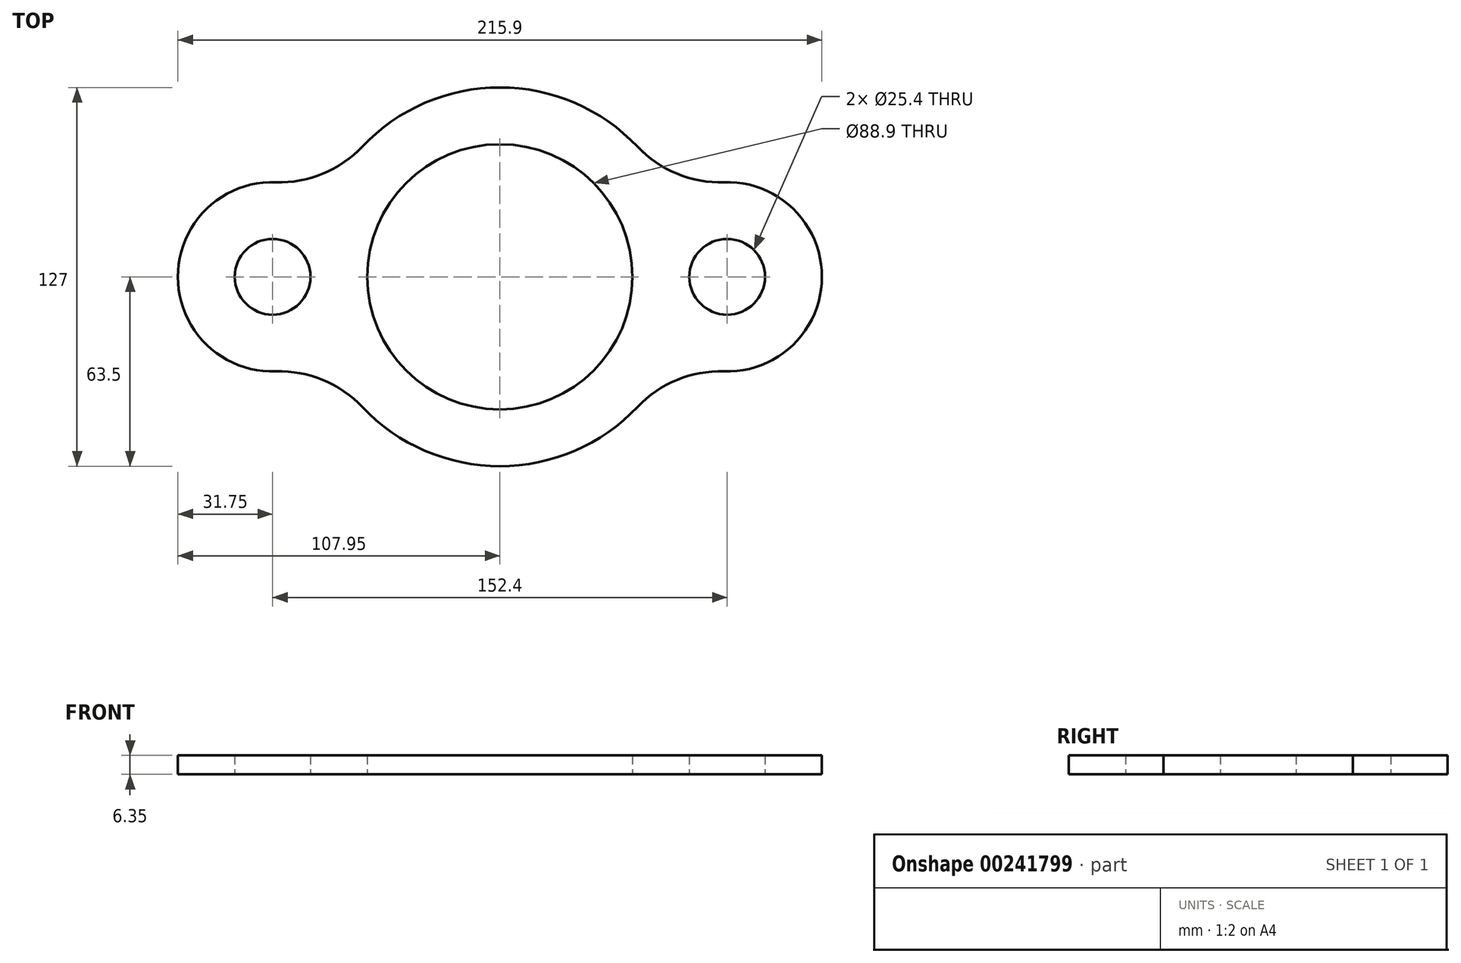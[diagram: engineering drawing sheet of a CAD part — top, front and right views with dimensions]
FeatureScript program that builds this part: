
annotation { "Feature Type Name" : "Feature", "Feature Type Description" : "" }
export const myFeature = defineFeature(function(context is Context, id is Id, definition is map)
    precondition{}
    {
        {
            var Q0;
            Q0=qCreatedBy(makeId("Top.planeOp"),FACE);
            var sketch = newSketch(context, id + "F0", { "sketchPlane" : qUnion([Q0])});
            skCircle(sketch, "E0", {"center": v(76.2, 0) * mm, "radius": 12.7 * mm});
            skCircle(sketch, "E1", {"center": v(0, 0) * mm, "radius": 44.45 * mm});
            skCircle(sketch, "E2", {"center": v(-76.2, 0) * mm, "radius": 12.7 * mm});
            skArc(sketch, "E3.MirrorC", {"start": v(75.12, 31.73) * mm, "mid": v(107.95, 0) * mm, "end": v(75.12, -31.73) * mm});
            skArc(sketch, "E4.MirrorC", {"start": v(-75.12, 31.73) * mm, "mid": v(-107.95, 0) * mm, "end": v(-75.12, -31.73) * mm});
            skArc(sketch, "E5", {"start": v(-46.14, -43.63) * mm, "mid": v(0, -63.5) * mm, "end": v(46.14, -43.63) * mm});
            skArc(sketch, "E6.trimOffspring", {"start": v(46.14, 43.63) * mm, "mid": v(0, 63.5) * mm, "end": v(-46.14, 43.63) * mm});
            skArc(sketch, "E7.filletArc", {"start": v(-75.12, 31.73) * mm, "mid": v(-59.35, 34.56) * mm, "end": v(-46.14, 43.63) * mm});
            skArc(sketch, "E8.MirrorCS", {"start": v(75.12, 31.73) * mm, "mid": v(59.35, 34.56) * mm, "end": v(46.14, 43.63) * mm});
            skArc(sketch, "E9.MirrorCS", {"start": v(75.12, -31.73) * mm, "mid": v(59.35, -34.56) * mm, "end": v(46.14, -43.63) * mm});
            skArc(sketch, "E10.MirrorCS", {"start": v(-75.12, -31.73) * mm, "mid": v(-59.35, -34.56) * mm, "end": v(-46.14, -43.63) * mm});
            skSolve(sketch);
        }
        {
            var Q0;
            Q0=makeQuery(id+"F0.imprint","IMPRINT",FACE,{"disambiguationData":[TD([[makeQuery(id+"F0.imprint","IMPRINT",EDGE,{"derivedFrom":sQuery(id+"F0.wireOp",EDGE,"E0")}),-1.0]])]});
            extrude(context, id + "F1", {"entities" : qUnion([Q0]), "depth" : 6.35 * mm});
        }
    });
